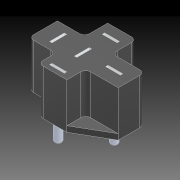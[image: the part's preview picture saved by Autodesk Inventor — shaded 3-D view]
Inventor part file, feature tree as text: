
AUTODESK INVENTOR PART (.ipt)
format: ipt  version: 2020 (Build 240168000, 168)  size: 152,576 bytes
history: native  units: mm
features: projected_geometry x2, other x1, extrude x1, sketch x1, fillet x1
ambient origin geometry x8: Origin, YZ Plane, XZ Plane, XY Plane, X Axis, Y Axis, Z Axis, Center Point
bodies: Body1 (feature_tree)
feature tree (6):
  other  "Твердое тело1"
  extrude  "Выдавливание1"  Depth=2.54mm TaperAngle=0.0deg
  sketch  "Эскиз1"
  projected_geometry  "Спроецированная петля1"
  projected_geometry  "Спроецированная петля2"
  fillet  "Fillet12"  [1 undecoded]
note: 1 required parameter value undecoded (feature->parameter linkage not recoverable at this tier; creation-order binding heuristic only, values carry confidence <= 0.55)
